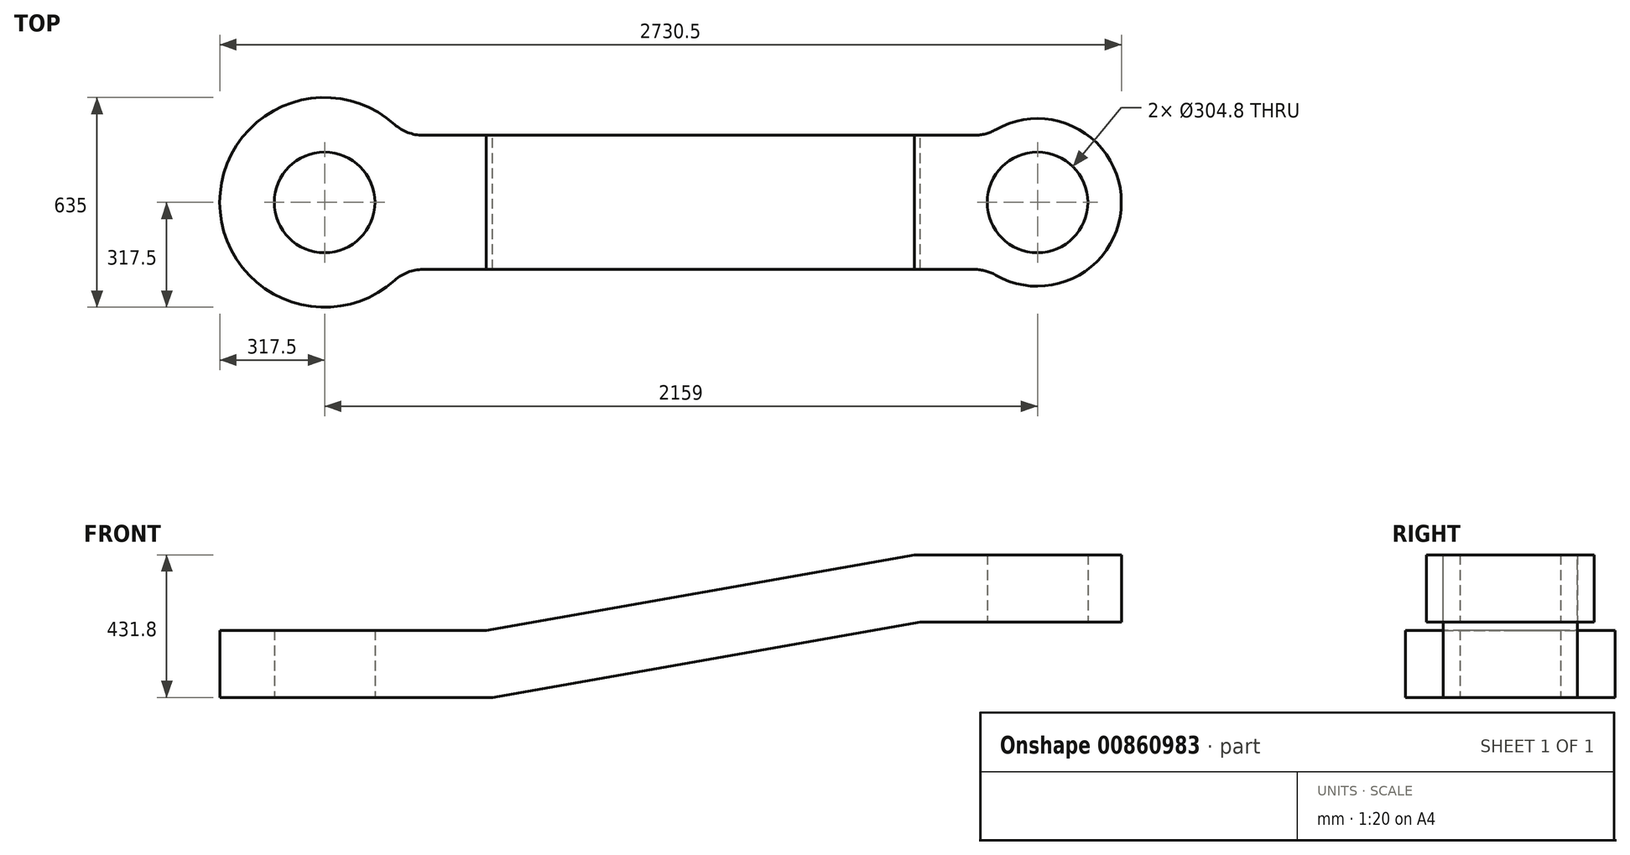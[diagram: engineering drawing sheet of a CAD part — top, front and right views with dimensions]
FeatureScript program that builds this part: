
annotation { "Feature Type Name" : "Feature", "Feature Type Description" : "" }
export const myFeature = defineFeature(function(context is Context, id is Id, definition is map)
    precondition{}
    {
        {
            var Q0;
            Q0=qCreatedBy(makeId("Top.planeOp"),FACE);
            var sketch = newSketch(context, id + "F0", { "sketchPlane" : qUnion([Q0])});
            skCircle(sketch, "E0", {"center": v(0, 0) * mm, "radius": 317.5 * mm});
            skCircle(sketch, "E1", {"center": v(2159, 0) * mm, "radius": 254 * mm});
            skLineSegment(sketch, "E2", {"start": v(0, 0) * mm, "end": v(2159, 0) * mm, "construction": true});
            skLineSegment(sketch, "E3", {"start": v(243.96, 203.2) * mm, "end": v(2006.6, 203.2) * mm});
            skLineSegment(sketch, "E4.MirrorCS", {"start": v(243.96, -203.2) * mm, "end": v(2006.6, -203.2) * mm});
            skCircle(sketch, "E5", {"center": v(0, 0) * mm, "radius": 152.4 * mm});
            skCircle(sketch, "E6", {"center": v(2159, 0) * mm, "radius": 152.4 * mm});
            skSolve(sketch);
        }
        {
            var Q0;
            Q0 = qSketchRegion(id + "F0", true);
            extrude(context, id + "F1", {"entities" : qUnion([Q0]), "depth" : 635 * mm, "offsetDistance" : 25.4 * mm});
        }
        {
            var Q0;
            Q0=qCreatedBy(makeId("Front.planeOp"),FACE);
            var sketch = newSketch(context, id + "F2", { "sketchPlane" : qUnion([Q0])});
            skLineSegment(sketch, "E7", {"start": v(-317.5, 0) * mm, "end": v(508, 0) * mm});
            skLineSegment(sketch, "E8", {"start": v(508, 0) * mm, "end": v(1804.46, 228.6) * mm});
            skLineSegment(sketch, "E9", {"start": v(1804.46, 228.6) * mm, "end": v(2413, 228.6) * mm});
            skLineSegment(sketch, "E10.0", {"start": v(1786.68, 431.8) * mm, "end": v(2413, 431.8) * mm});
            skLineSegment(sketch, "E10.1", {"start": v(490.22, 203.2) * mm, "end": v(1786.68, 431.8) * mm});
            skLineSegment(sketch, "E10.2", {"start": v(-317.5, 203.2) * mm, "end": v(490.22, 203.2) * mm});
            skLineSegment(sketch, "E11", {"start": v(-317.5, 203.2) * mm, "end": v(-317.5, 0) * mm});
            skLineSegment(sketch, "E12", {"start": v(2413, 431.8) * mm, "end": v(2413, 228.6) * mm});
            skLineSegment(sketch, "E13", {"start": v(-317.5, 0) * mm, "end": v(-317.5, 635) * mm});
            skLineSegment(sketch, "E14", {"start": v(2413, 635) * mm, "end": v(2413, 0) * mm});
            skSolve(sketch);
        }
        {
            var Q0;
            Q0 = qSketchRegion(id + "F2", true);
            extrude(context, id + "F3", {"entities" : qUnion([Q0]), "operationType" : NewBodyOperationType.INTERSECT, "endBound" : BoundingType.SYMMETRIC, "depth" : 635 * mm, "offsetDistance" : 25.4 * mm});
        }
        {
            var Q0;
            Q0=makeQuery(id+"F1.opExtrude","SWEPT_EDGE",EDGE,{"disambiguationData":[OSD([sQuery(id+"F0.wireOp",EDGE,"E1"),sQuery(id+"F0.wireOp",EDGE,"E3")])]});
            var Q1;
            Q1=makeQuery(id+"F1.opExtrude","SWEPT_EDGE",EDGE,{"disambiguationData":[OSD([sQuery(id+"F0.wireOp",EDGE,"E0"),sQuery(id+"F0.wireOp",EDGE,"E3")])]});
            var Q2;
            Q2=makeQuery(id+"F1.opExtrude","SWEPT_EDGE",EDGE,{"disambiguationData":[OSD([sQuery(id+"F0.wireOp",EDGE,"E0"),sQuery(id+"F0.wireOp",EDGE,"E4.MirrorCS")])]});
            var Q3;
            Q3=makeQuery(id+"F1.opExtrude","SWEPT_EDGE",EDGE,{"disambiguationData":[OSD([sQuery(id+"F0.wireOp",EDGE,"E1"),sQuery(id+"F0.wireOp",EDGE,"E4.MirrorCS")])]});
            fillet(context, id + "F4", {"entities" : qUnion([Q0, Q1, Q2, Q3]), "radius" : 127 * mm, "tangentPropagation" : true, "allowEdgeOverflow" : false});
        }
    });
